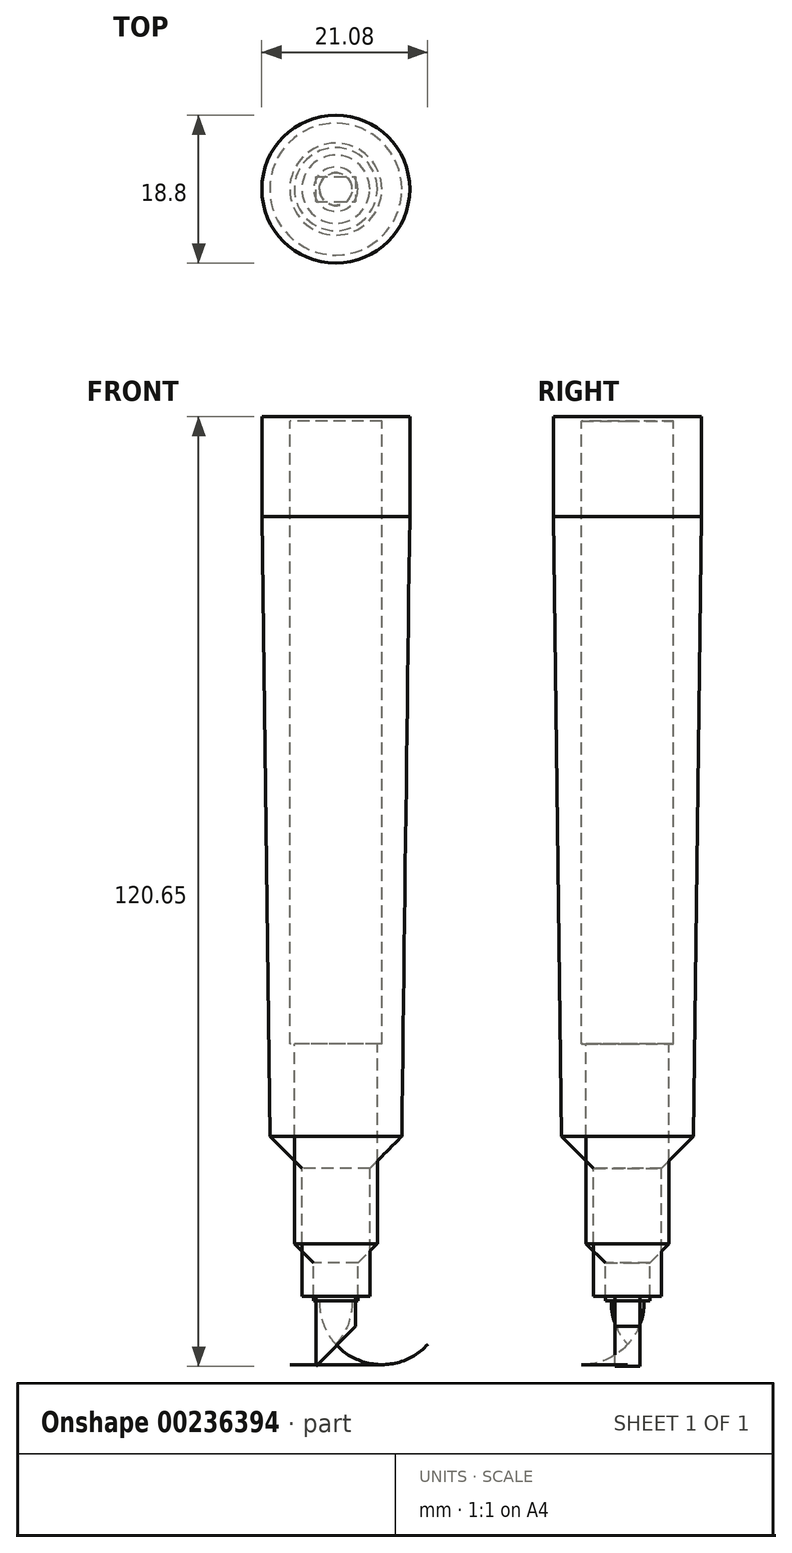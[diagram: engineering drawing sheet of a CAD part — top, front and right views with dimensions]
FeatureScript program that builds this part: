
annotation { "Feature Type Name" : "Feature", "Feature Type Description" : "" }
export const myFeature = defineFeature(function(context is Context, id is Id, definition is map)
    precondition{}
    {
        {
            var Q0;
            Q0=qCreatedBy(makeId("Front.planeOp"),FACE);
            var sketch = newSketch(context, id + "F0", { "sketchPlane" : qUnion([Q0])});
            skLineSegment(sketch, "E0.bottom", {"start": v(0, 6.1) * mm, "end": v(9.4, 6.1) * mm});
            skLineSegment(sketch, "E0.top", {"start": v(0, 117.86) * mm, "end": v(9.4, 117.86) * mm});
            skLineSegment(sketch, "E0.left", {"start": v(0, 6.1) * mm, "end": v(0, 117.86) * mm});
            skLineSegment(sketch, "E0.right", {"start": v(9.4, 6.1) * mm, "end": v(9.4, 117.86) * mm});
            skLineSegment(sketch, "E1", {"start": v(0, 0) * mm, "end": v(0, -42.81) * mm, "construction": true});
            skLineSegment(sketch, "E2", {"start": v(4.32, 6.1) * mm, "end": v(4.32, 22.35) * mm});
            skLineSegment(sketch, "E3", {"start": v(4.32, 22.35) * mm, "end": v(8.38, 26.42) * mm});
            skLineSegment(sketch, "E4", {"start": v(8.38, 26.42) * mm, "end": v(9.4, 105.16) * mm});
            skSolve(sketch);
        }
        {
            var Q0;
            {var subQ1=sQuery(id+"F0.wireOp",EDGE,"E0.top");Q0=makeQuery(id+"F0.imprint","IMPRINT",FACE,{"disambiguationData":[TD([[makeQuery(id+"F0.imprint","IMPRINT",EDGE,{"derivedFrom":subQ1}),-1.0]])]});}
            var Q1;
            Q1=sQuery(id+"F0.wireOp",EDGE,"E1");
            revolve(context, id + "F1", {"entities" : qUnion([Q0]), "axis" : qUnion([Q1]), "revolveType" : RevolveType.FULL});
        }
        {
            var Q0;
            Q0=qCreatedBy(makeId("Front.planeOp"),FACE);
            var sketch = newSketch(context, id + "F2", { "sketchPlane" : qUnion([Q0])});
            skLineSegment(sketch, "E5", {"start": v(-2.54, 8.68) * mm, "end": v(-2.54, -2.8) * mm});
            skLineSegment(sketch, "E6", {"start": v(-2.54, -2.8) * mm, "end": v(2.54, 2.29) * mm});
            skLineSegment(sketch, "E7", {"start": v(2.54, 2.29) * mm, "end": v(2.54, 8.68) * mm});
            skLineSegment(sketch, "E8", {"start": v(2.54, 8.68) * mm, "end": v(-2.54, 8.68) * mm});
            skPoint(sketch, "E9", {"position": v(0, -0.25) * mm});
            skSolve(sketch);
        }
        {
            var Q0;
            Q0=makeQuery(id+"F2.imprint","IMPRINT",FACE,{"disambiguationData":[TD([[makeQuery(id+"F2.imprint","IMPRINT",EDGE,{"derivedFrom":sQuery(id+"F2.wireOp",EDGE,"E5")}),1.0]])]});
            extrude(context, id + "F3", {"entities" : qUnion([Q0]), "operationType" : NewBodyOperationType.ADD, "endBound" : BoundingType.SYMMETRIC, "depth" : 3.17 * mm});
        }
        {
            var Q0;
            Q0=qCreatedBy(makeId("Front.planeOp"),FACE);
            var sketch = newSketch(context, id + "F4", { "sketchPlane" : qUnion([Q0])});
            skLineSegment(sketch, "E10", {"start": v(0, 0) * mm, "end": v(0, -51.94) * mm, "construction": true});
            skLineSegment(sketch, "E11.bottom", {"start": v(0, 5.51) * mm, "end": v(5.84, 5.51) * mm});
            skLineSegment(sketch, "E11.top", {"start": v(0, 117.27) * mm, "end": v(5.84, 117.27) * mm});
            skLineSegment(sketch, "E11.left", {"start": v(0, 5.51) * mm, "end": v(0, 117.27) * mm});
            skLineSegment(sketch, "E11.right", {"start": v(5.84, 5.51) * mm, "end": v(5.84, 117.27) * mm});
            skLineSegment(sketch, "E12", {"start": v(2.8, 5.51) * mm, "end": v(2.8, 10.34) * mm});
            skLineSegment(sketch, "E13", {"start": v(2.8, 10.34) * mm, "end": v(5.27, 12.8) * mm});
            skLineSegment(sketch, "E14", {"start": v(5.27, 12.8) * mm, "end": v(5.27, 38.15) * mm});
            skLineSegment(sketch, "E15", {"start": v(5.27, 38.15) * mm, "end": v(5.84, 38.15) * mm});
            skArc(sketch, "E16", {"start": v(0, 0) * mm, "mid": v(1.57, 2.56) * mm, "end": v(2.08, 5.51) * mm});
            skLineSegment(sketch, "E17", {"start": v(0, 5.51) * mm, "end": v(0, 0) * mm});
            skSolve(sketch);
        }
        {
            var Q0;
            {var subQ0=sQuery(id+"F4.wireOp",EDGE,"E11.top");Q0=makeQuery(id+"F4.imprint","IMPRINT",FACE,{"disambiguationData":[TD([[makeQuery(id+"F4.imprint","IMPRINT",EDGE,{"derivedFrom":subQ0}),-1.0]])]});}
            var Q1;
            {var subQ2=sQuery(id+"F4.wireOp",EDGE,"E16");Q1=makeQuery(id+"F4.imprint","IMPRINT",FACE,{"disambiguationData":[TD([[makeQuery(id+"F4.imprint","IMPRINT",EDGE,{"derivedFrom":subQ2}),1.0]])]});}
            var Q2;
            Q2=sQuery(id+"F4.wireOp",EDGE,"E10");
            revolve(context, id + "F5", {"entities" : qUnion([Q0, Q1]), "axis" : qUnion([Q2]), "revolveType" : RevolveType.FULL});
        }
    });
